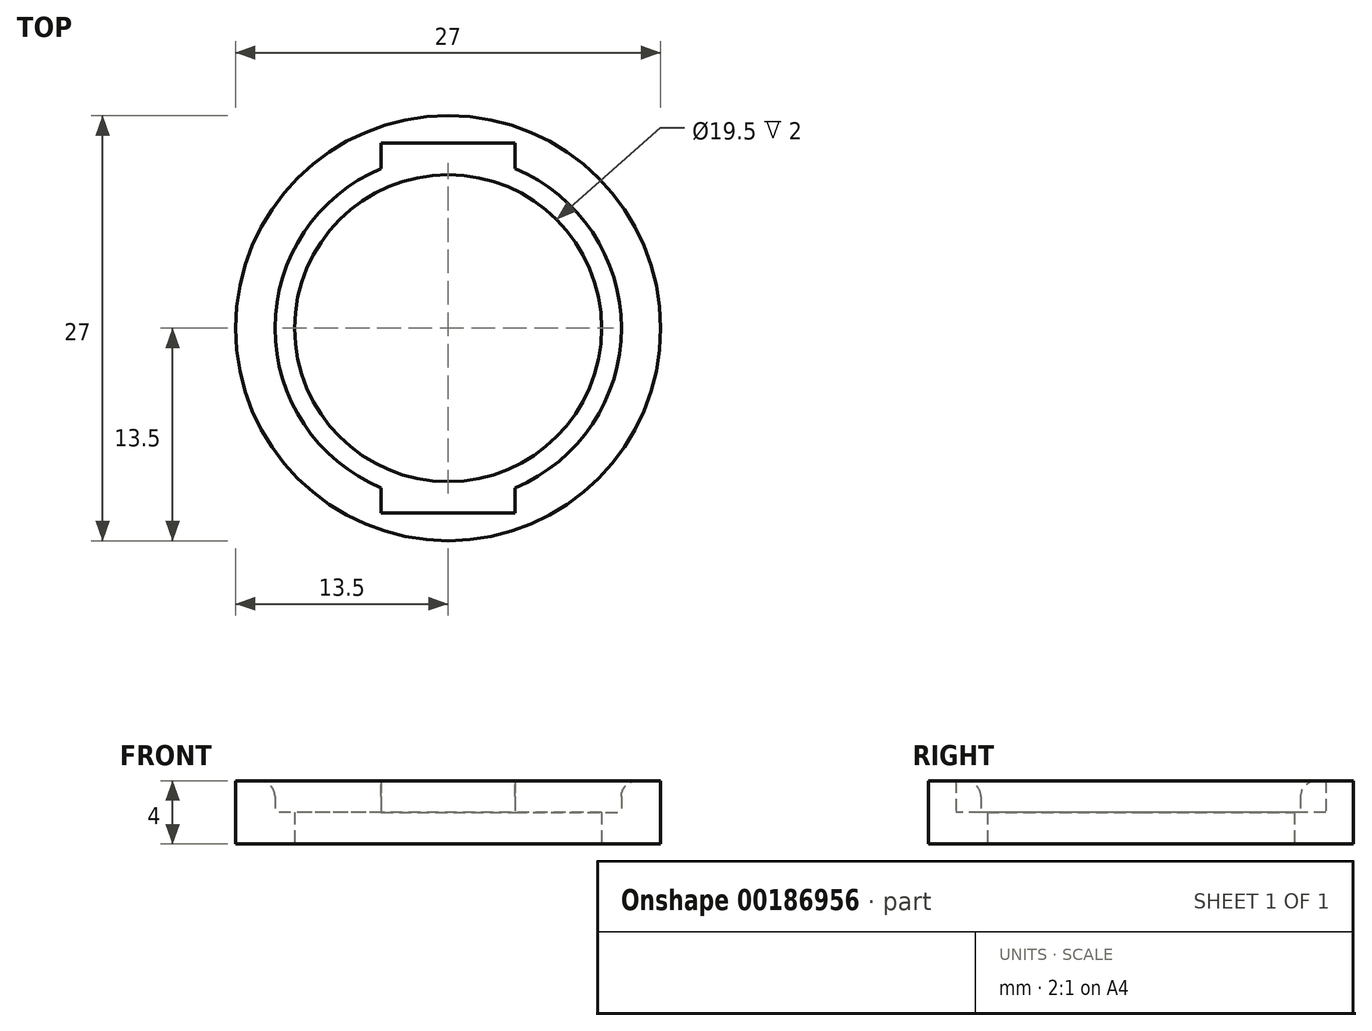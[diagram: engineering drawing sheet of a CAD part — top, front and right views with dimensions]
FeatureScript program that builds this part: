
annotation { "Feature Type Name" : "Feature", "Feature Type Description" : "" }
export const myFeature = defineFeature(function(context is Context, id is Id, definition is map)
    precondition{}
    {
        {
            var Q0;
            Q0=qCreatedBy(makeId("Top.planeOp"),FACE);
            var sketch = newSketch(context, id + "F0", { "sketchPlane" : qUnion([Q0])});
            skCircle(sketch, "E0", {"center": v(0, 0) * mm, "radius": 13.5 * mm});
            skCircle(sketch, "E1", {"center": v(0, 0) * mm, "radius": 11 * mm});
            skLineSegment(sketch, "E2.bottom", {"start": v(-4.25, 11.75) * mm, "end": v(4.25, 11.75) * mm});
            skLineSegment(sketch, "E2.top", {"start": v(-4.25, -11.75) * mm, "end": v(4.25, -11.75) * mm});
            skLineSegment(sketch, "E2.left", {"start": v(-4.25, 11.75) * mm, "end": v(-4.25, -11.75) * mm});
            skLineSegment(sketch, "E2.right", {"start": v(4.25, 11.75) * mm, "end": v(4.25, -11.75) * mm});
            skLineSegment(sketch, "E3", {"start": v(-4.25, -11.75) * mm, "end": v(4.25, 11.75) * mm});
            skSolve(sketch);
        }
        {
            var Q0;
            Q0=makeQuery(id+"F0.imprint","IMPRINT",FACE,{"disambiguationData":[TD([[makeQuery(id+"F0.imprint","IMPRINT",EDGE,{"derivedFrom":sQuery(id+"F0.wireOp",EDGE,"E0")}),1.0]])]});
            extrude(context, id + "F1", {"entities" : qUnion([Q0]), "depth" : 4 * mm});
        }
        {
            var Q0;
            Q0=qCreatedBy(makeId("Top.planeOp"),FACE);
            var sketch = newSketch(context, id + "F2", { "sketchPlane" : qUnion([Q0])});
            skCircle(sketch, "E4", {"center": v(0, 0) * mm, "radius": 9.75 * mm});
            skCircle(sketch, "E5", {"center": v(0, 0) * mm, "radius": 13.5 * mm});
            skSolve(sketch);
        }
        {
            var Q0;
            Q0=makeQuery(id+"F2.imprint","IMPRINT",FACE,{"disambiguationData":[TD([[makeQuery(id+"F2.imprint","IMPRINT",EDGE,{"derivedFrom":sQuery(id+"F2.wireOp",EDGE,"E4")}),-1.0]])]});
            extrude(context, id + "F3", {"entities" : qUnion([Q0]), "operationType" : NewBodyOperationType.ADD, "depth" : 2 * mm});
        }
        {
            var Q0;
            {var subQ0=sQuery(id+"F0.wireOp",EDGE,"E2.right");var subQ1=sQuery(id+"F0.wireOp",EDGE,"E1");Q0=makeQuery(id+"F1.opExtrude","CAP_EDGE",EDGE,{"disambiguationData":[OSD([subQ1]),TDD([makeQuery(id+"F0.imprint","IMPRINT",EDGE,{"disambiguationData":[TD([[makeQuery(id+"F0.imprint","INTERSECT",VERTEX,{"disambiguationData":[OD(0.0)],"derivedFrom":[subQ1,subQ0]}),1.0]])],"derivedFrom":subQ1})])],"isStart":false});}
            var Q1;
            {var subQ0=sQuery(id+"F0.wireOp",EDGE,"E2.left");var subQ1=sQuery(id+"F0.wireOp",EDGE,"E1");Q1=makeQuery(id+"F1.opExtrude","CAP_EDGE",EDGE,{"disambiguationData":[OSD([subQ1]),TDD([makeQuery(id+"F0.imprint","IMPRINT",EDGE,{"disambiguationData":[TD([[makeQuery(id+"F0.imprint","INTERSECT",VERTEX,{"disambiguationData":[OD(0.0)],"derivedFrom":[subQ1,subQ0]}),-1.0]])],"derivedFrom":subQ1})])],"isStart":false});}
            fillet(context, id + "F4", {"entities" : qUnion([Q0, Q1]), "radius" : 1 * mm, "tangentPropagation" : true, "allowEdgeOverflow" : false});
        }
    });
